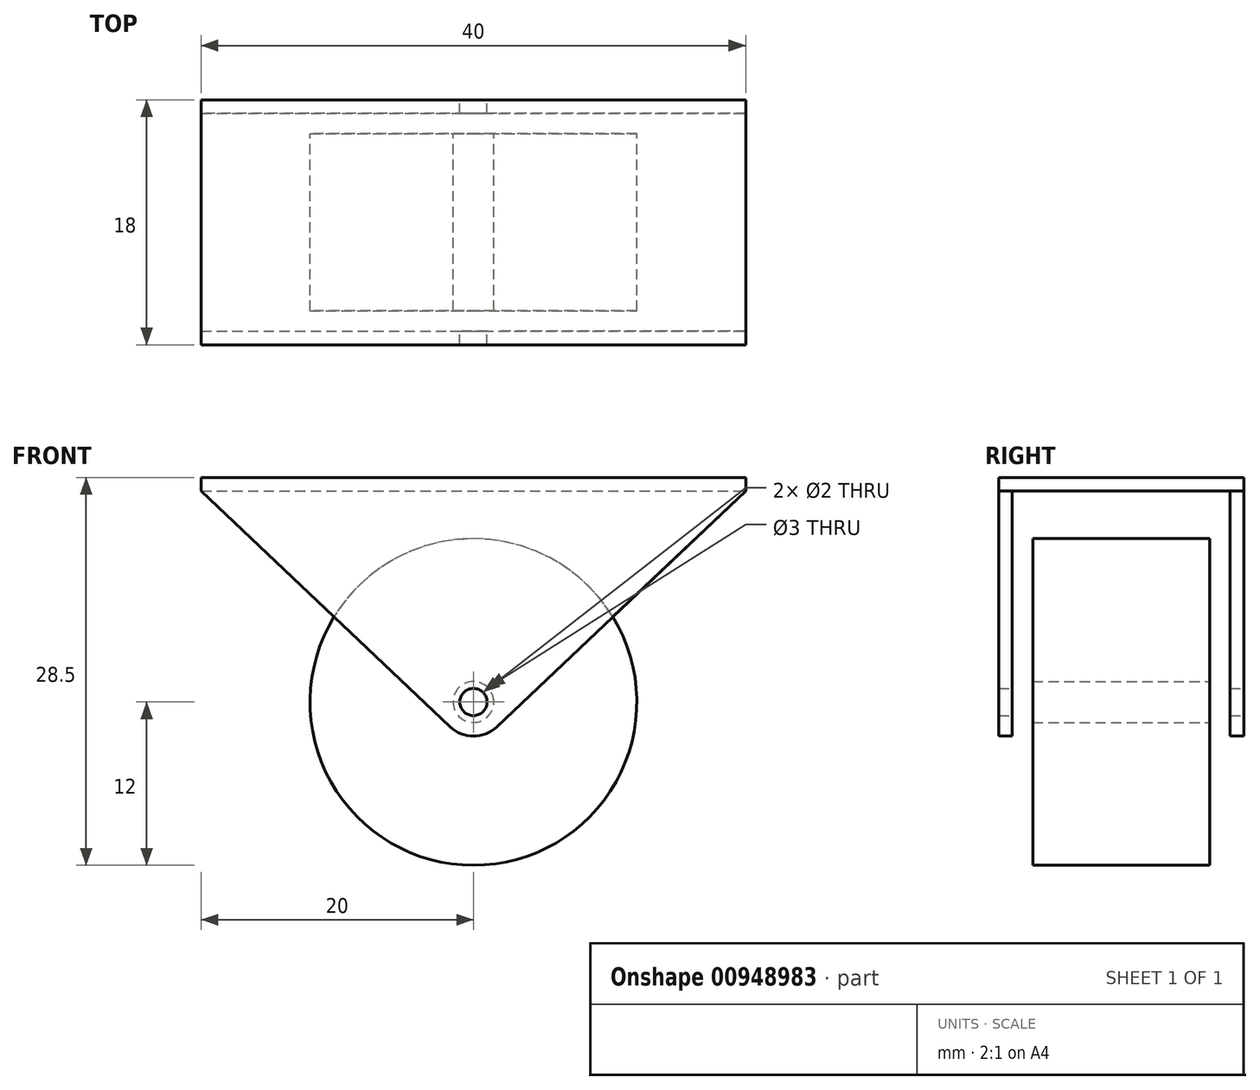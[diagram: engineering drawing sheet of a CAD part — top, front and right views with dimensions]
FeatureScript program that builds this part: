
annotation { "Feature Type Name" : "Feature", "Feature Type Description" : "" }
export const myFeature = defineFeature(function(context is Context, id is Id, definition is map)
    precondition{}
    {
        {
            var Q0;
            Q0=qCreatedBy(makeId("Front.planeOp"),FACE);
            var sketch = newSketch(context, id + "F0", { "sketchPlane" : qUnion([Q0])});
            skCircle(sketch, "E0", {"center": v(0, 0) * mm, "radius": 12 * mm});
            skCircle(sketch, "E1", {"center": v(0, 0) * mm, "radius": 1.5 * mm});
            skSolve(sketch);
        }
        {
            var Q0;
            Q0=qSketchRegion(id+"F0",true);
            extrude(context, id + "F1", {"entities" : qUnion([Q0]), "depth" : 6.5 * mm, "offsetDistance" : 25 * mm, "hasSecondDirection" : true, "secondDirectionOppositeDirection" : true, "secondDirectionDepth" : 6.5 * mm});
        }
        {
            var Q0;
            Q0=qCreatedBy(makeId("Top.planeOp"),FACE);
            cPlane(context, id + "F2", {"entities" : qUnion([Q0]), "cplaneType" : CPlaneType.OFFSET, "offset" : (28 - 11.5) * mm, "width" : 150 * mm, "height" : 150 * mm});
        }
        {
            var Q0;
            Q0=qCreatedBy(id+"F2.planeOp",FACE);
            var sketch = newSketch(context, id + "F3", { "sketchPlane" : qUnion([Q0])});
            skLineSegment(sketch, "E2.bottom", {"start": v(-20, 9) * mm, "end": v(20, 9) * mm});
            skLineSegment(sketch, "E2.top", {"start": v(-20, -9) * mm, "end": v(20, -9) * mm});
            skLineSegment(sketch, "E2.left", {"start": v(-20, 9) * mm, "end": v(-20, -9) * mm});
            skLineSegment(sketch, "E2.right", {"start": v(20, 9) * mm, "end": v(20, -9) * mm});
            skPoint(sketch, "E3", {"position": v(-20, 0) * mm});
            skPoint(sketch, "E4", {"position": v(0, -9) * mm});
            skSolve(sketch);
        }
        {
            var Q0;
            Q0=qSketchRegion(id+"F3",true);
            extrude(context, id + "F4", {"entities" : qUnion([Q0]), "oppositeDirection" : true, "depth" : 1 * mm, "offsetDistance" : 25 * mm});
        }
        {
            var Q0;
            Q0=makeQuery(id+"F4.opExtrude","SWEPT_FACE",FACE,{"disambiguationData":[OSD([sQuery(id+"F3.wireOp",EDGE,"E2.top")])]});
            var sketch = newSketch(context, id + "F5", { "sketchPlane" : qUnion([Q0])});
            skCircle(sketch, "E5", {"center": v(0, 0) * mm, "radius": 2.5 * mm});
            skLineSegment(sketch, "E6", {"start": v(-20, 15.5) * mm, "end": v(-1.72, -1.82) * mm});
            skLineSegment(sketch, "E7", {"start": v(20, 15.5) * mm, "end": v(1.72, -1.82) * mm});
            skSolve(sketch);
        }
        {
            var Q0;
            {var subQ0=sQuery(id+"F5.wireOp",EDGE,"E6");Q0=makeQuery(id+"F5.imprint","IMPRINT",FACE,{"disambiguationData":[TD([[makeQuery(id+"F5.imprint","IMPRINT",EDGE,{"derivedFrom":subQ0}),1.0]])]});}
            var Q1;
            {var subQ0=sQuery(id+"F5.wireOp",EDGE,"E5");var subQ1=makeQuery(id+"F5.imprint","INTERSECT",VERTEX,{"derivedFrom":[subQ0,sQuery(id+"F5.wireOp",EDGE,"E6")]});Q1=makeQuery(id+"F5.imprint","IMPRINT",FACE,{"disambiguationData":[TD([[makeQuery(id+"F5.imprint","IMPRINT",EDGE,{"disambiguationData":[TD([[subQ1,-1.0]])],"derivedFrom":subQ0}),1.0]])]});}
            extrude(context, id + "F6", {"entities" : qUnion([Q0, Q1]), "operationType" : NewBodyOperationType.ADD, "oppositeDirection" : true, "depth" : 1 * mm, "offsetDistance" : 25 * mm});
        }
        {
            var Q0;
            Q0=makeQuery(id+"F4.opExtrude","SWEPT_FACE",FACE,{"disambiguationData":[OSD([sQuery(id+"F3.wireOp",EDGE,"E2.bottom")])]});
            var sketch = newSketch(context, id + "F7", { "sketchPlane" : qUnion([Q0])});
            skLineSegment(sketch, "E8.0.0", {"start": v(1.72, -1.82) * mm, "end": v(20, 15.5) * mm});
            skLineSegment(sketch, "E8.0.1", {"start": v(20, 15.5) * mm, "end": v(-20, 15.5) * mm});
            skLineSegment(sketch, "E8.0.2", {"start": v(-20, 15.5) * mm, "end": v(-1.72, -1.82) * mm});
            skArc(sketch, "E8.0.3", {"start": v(-1.72, -1.82) * mm, "mid": v(0, -2.5) * mm, "end": v(1.72, -1.82) * mm});
            skSolve(sketch);
        }
        {
            var Q0;
            Q0=qSketchRegion(id+"F7",true);
            extrude(context, id + "F8", {"entities" : qUnion([Q0]), "operationType" : NewBodyOperationType.ADD, "oppositeDirection" : true, "depth" : 1 * mm, "offsetDistance" : 25 * mm});
        }
        {
            var Q0;
            Q0=makeQuery(id+"F8.boolean.opBoolean","MERGE",FACE,{"derivedFrom":[makeQuery(id+"F4.opExtrude","SWEPT_FACE",FACE,{"disambiguationData":[OSD([sQuery(id+"F3.wireOp",EDGE,"E2.bottom")])]}),makeQuery(id+"F8.opExtrude","CAP_FACE",FACE,{"disambiguationData":[OSD([sQuery(id+"F7.wireOp",EDGE,"E8.0.0"),sQuery(id+"F7.wireOp",EDGE,"E8.0.1"),sQuery(id+"F7.wireOp",EDGE,"E8.0.2"),sQuery(id+"F7.wireOp",EDGE,"E8.0.3")])],"isStart":true})]});
            var sketch = newSketch(context, id + "F9", { "sketchPlane" : qUnion([Q0])});
            skCircle(sketch, "E9", {"center": v(0, 0) * mm, "radius": 1 * mm});
            skSolve(sketch);
        }
        {
            var Q0;
            Q0=qSketchRegion(id+"F9",true);
            extrude(context, id + "F10", {"entities" : qUnion([Q0]), "operationType" : NewBodyOperationType.REMOVE, "endBound" : BoundingType.THROUGH_ALL, "oppositeDirection" : true, "depth" : 25 * mm, "offsetDistance" : 25 * mm});
        }
    });
